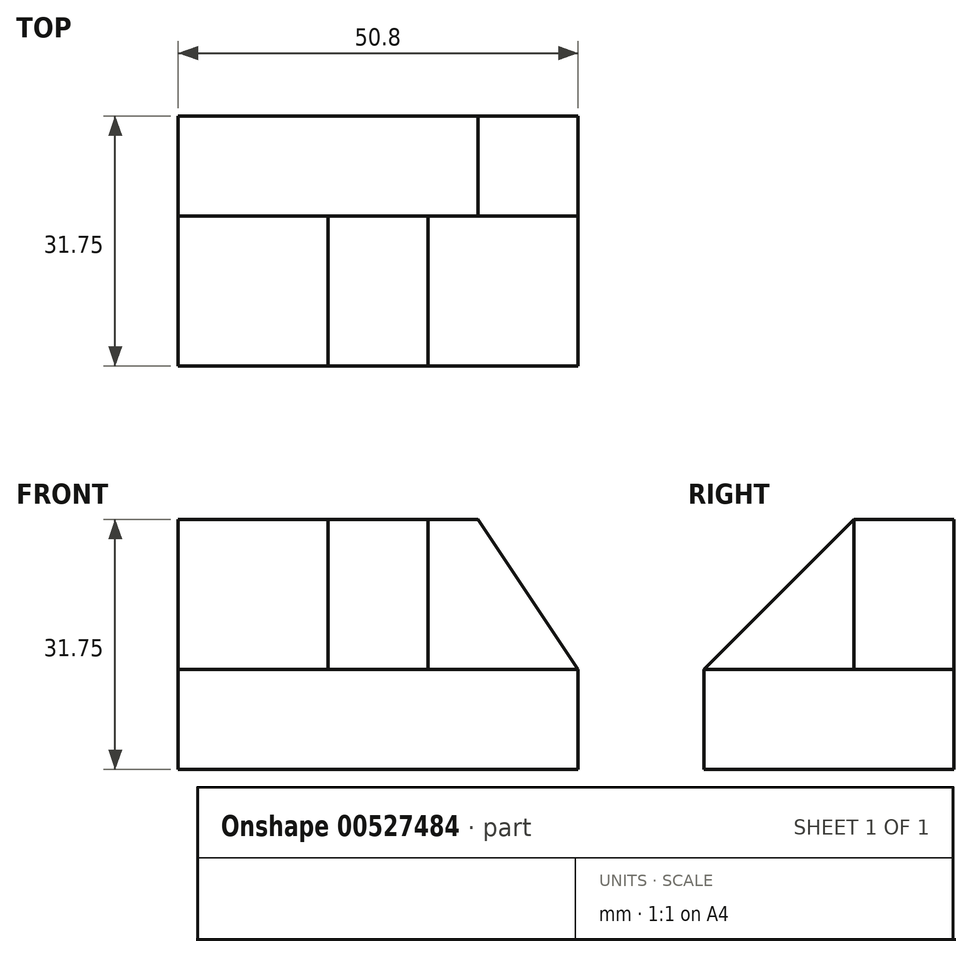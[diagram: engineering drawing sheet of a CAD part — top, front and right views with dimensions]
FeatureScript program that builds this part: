
annotation { "Feature Type Name" : "Feature", "Feature Type Description" : "" }
export const myFeature = defineFeature(function(context is Context, id is Id, definition is map)
    precondition{}
    {
        {
            var Q0;
            Q0=qCreatedBy(makeId("Front.planeOp"),FACE);
            var sketch = newSketch(context, id + "F0", { "sketchPlane" : qUnion([Q0])});
            skLineSegment(sketch, "E0", {"start": v(0, 0) * mm, "end": v(0, 31.75) * mm});
            skLineSegment(sketch, "E1", {"start": v(0, 31.75) * mm, "end": v(50.8, 31.75) * mm});
            skLineSegment(sketch, "E2", {"start": v(50.8, 31.75) * mm, "end": v(50.8, 0) * mm});
            skLineSegment(sketch, "E3", {"start": v(50.8, 0) * mm, "end": v(0, 0) * mm});
            skSolve(sketch);
        }
        {
            var Q0;
            Q0 = qSketchRegion(id + "F0", true);
            extrude(context, id + "F1", {"entities" : qUnion([Q0]), "oppositeDirection" : true, "depth" : 31.75 * mm, "offsetDistance" : 25.4 * mm});
        }
        {
            var Q0;
            Q0=makeQuery(id+"F1.opExtrude","SWEPT_FACE",FACE,{"disambiguationData":[OSD([sQuery(id+"F0.wireOp",EDGE,"E1")])]});
            var sketch = newSketch(context, id + "F2", { "sketchPlane" : qUnion([Q0])});
            skLineSegment(sketch, "E4", {"start": v(0, 19.05) * mm, "end": v(50.8, 19.05) * mm});
            skLineSegment(sketch, "E5", {"start": v(19.05, 19.05) * mm, "end": v(19.05, 0) * mm});
            skLineSegment(sketch, "E6", {"start": v(31.75, 19.05) * mm, "end": v(31.75, 0) * mm});
            skSolve(sketch);
        }
        {
            var Q0;
            {var subQ4=sQuery(id+"F2.wireOp",EDGE,"E5");Q0=makeQuery(id+"F2.imprint","IMPRINT",FACE,{"disambiguationData":[TD([[makeQuery(id+"F2.imprint","IMPRINT",EDGE,{"derivedFrom":subQ4}),-1.0]])]});}
            extrude(context, id + "F3", {"entities" : qUnion([Q0]), "operationType" : NewBodyOperationType.REMOVE, "oppositeDirection" : true, "depth" : 19.05 * mm, "offsetDistance" : 25.4 * mm});
        }
        {
            var Q0;
            {var subQ4=sQuery(id+"F2.wireOp",EDGE,"E6");Q0=makeQuery(id+"F2.imprint","IMPRINT",FACE,{"disambiguationData":[TD([[makeQuery(id+"F2.imprint","IMPRINT",EDGE,{"derivedFrom":subQ4}),1.0]])]});}
            extrude(context, id + "F4", {"entities" : qUnion([Q0]), "operationType" : NewBodyOperationType.REMOVE, "oppositeDirection" : true, "depth" : 19.05 * mm, "offsetDistance" : 25.4 * mm});
        }
        {
            var Q0;
            Q0=makeQuery(id+"F4.boolean.opBoolean","COPY",FACE,{"derivedFrom":makeQuery(id+"F4.opExtrude","SWEPT_FACE",FACE,{"disambiguationData":[OSD([sQuery(id+"F2.wireOp",EDGE,"E6")])]})});
            var sketch = newSketch(context, id + "F5", { "sketchPlane" : qUnion([Q0])});
            skLineSegment(sketch, "E7", {"start": v(19.05, 31.75) * mm, "end": v(0, 12.7) * mm});
            skSolve(sketch);
        }
        {
            var Q0;
            Q0=makeQuery(id+"F5.imprint","IMPRINT",FACE,{"disambiguationData":[TD([[makeQuery(id+"F5.imprint","IMPRINT",EDGE,{"derivedFrom":sQuery(id+"F5.wireOp",EDGE,"E7")}),-1.0]])]});
            extrude(context, id + "F6", {"entities" : qUnion([Q0]), "operationType" : NewBodyOperationType.REMOVE, "oppositeDirection" : true, "depth" : 25.4 * mm, "offsetDistance" : 25.4 * mm});
        }
        {
            var Q0;
            Q0=makeQuery(id+"F4.boolean.opBoolean","COPY",FACE,{"derivedFrom":makeQuery(id+"F4.opExtrude","SWEPT_FACE",FACE,{"disambiguationData":[OSD([sQuery(id+"F2.wireOp",EDGE,"E4")])]})});
            var sketch = newSketch(context, id + "F7", { "sketchPlane" : qUnion([Q0])});
            skLineSegment(sketch, "E8", {"start": v(38.1, 31.75) * mm, "end": v(50.8, 12.7) * mm});
            skSolve(sketch);
        }
        {
            var Q0;
            {var subQ0=sQuery(id+"F7.wireOp",EDGE,"E8");Q0=makeQuery(id+"F7.imprint","IMPRINT",FACE,{"disambiguationData":[TD([[makeQuery(id+"F7.imprint","IMPRINT",EDGE,{"derivedFrom":subQ0}),1.0]])]});}
            extrude(context, id + "F8", {"entities" : qUnion([Q0]), "operationType" : NewBodyOperationType.REMOVE, "oppositeDirection" : true, "depth" : 25.4 * mm, "offsetDistance" : 25.4 * mm});
        }
    });
